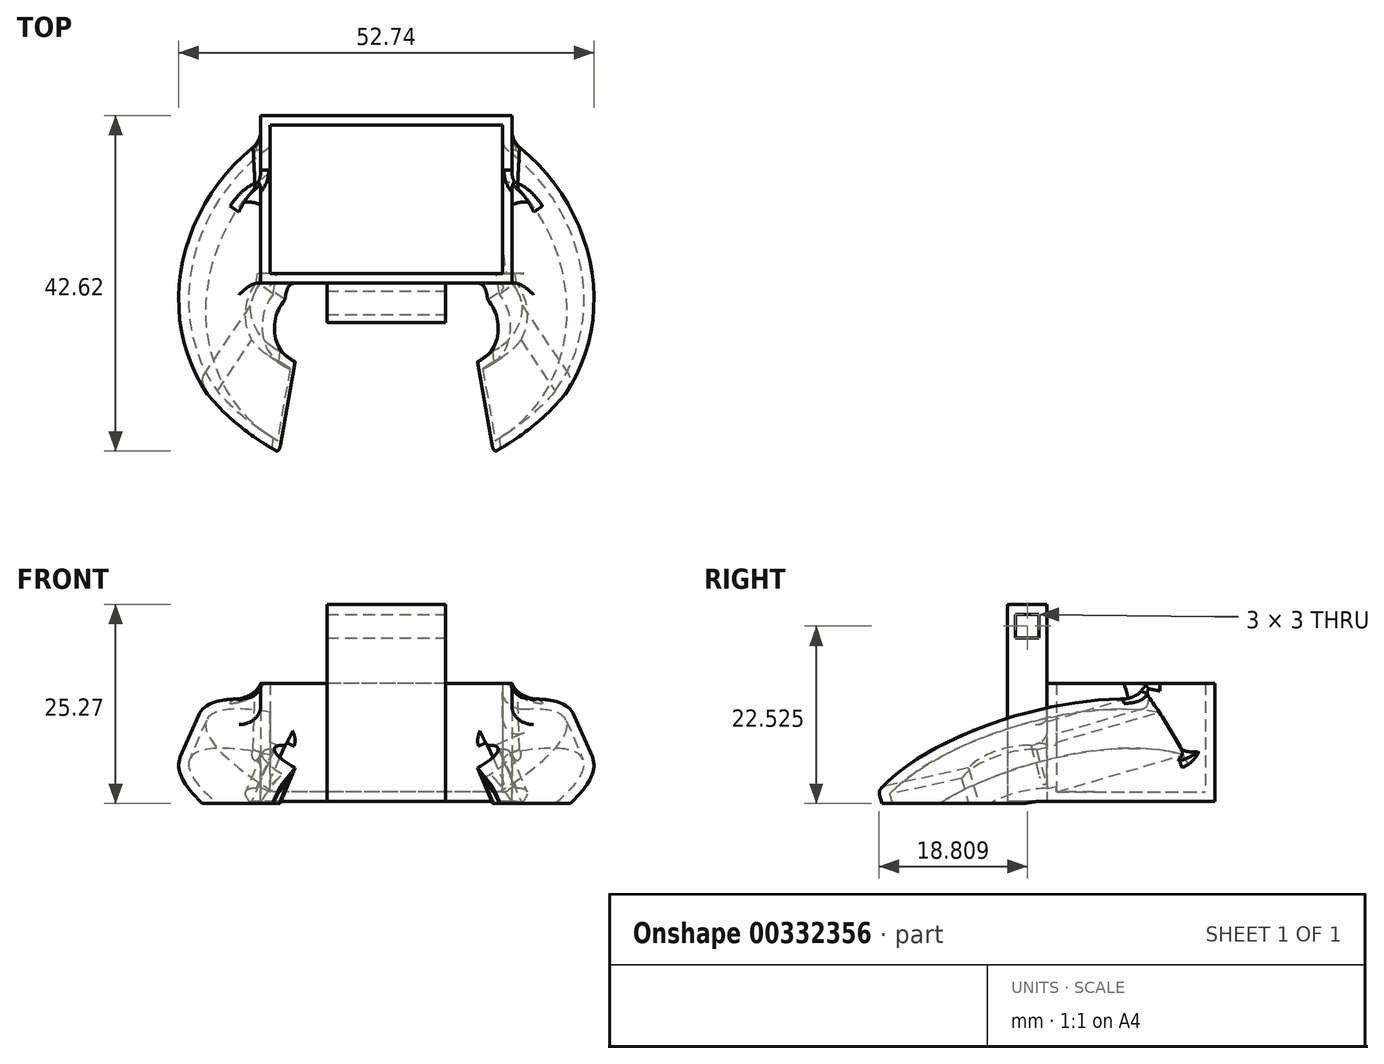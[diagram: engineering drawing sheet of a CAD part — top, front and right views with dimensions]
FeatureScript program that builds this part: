
annotation { "Feature Type Name" : "Feature", "Feature Type Description" : "" }
export const myFeature = defineFeature(function(context is Context, id is Id, definition is map)
    precondition{}
    {
        {
            var Q0;
            Q0=qCreatedBy(makeId("Top.planeOp"),FACE);
            var sketch = newSketch(context, id + "F0", { "sketchPlane" : qUnion([Q0])});
            skLineSegment(sketch, "E0.bottom", {"start": v(15.95, -10.65) * mm, "end": v(-15.95, -10.65) * mm});
            skLineSegment(sketch, "E0.top", {"start": v(15.95, 10.65) * mm, "end": v(-15.95, 10.65) * mm});
            skLineSegment(sketch, "E0.left", {"start": v(15.95, -10.65) * mm, "end": v(15.95, 10.65) * mm});
            skLineSegment(sketch, "E0.right", {"start": v(-15.95, -10.65) * mm, "end": v(-15.95, 10.65) * mm});
            skPoint(sketch, "E0.middle", {"position": v(0, 0) * mm});
            skLineSegment(sketch, "E1", {"start": v(-13, -24.65) * mm, "end": v(-13, -18.65) * mm});
            skLineSegment(sketch, "E2", {"start": v(-13, -24.65) * mm, "end": v(-13, -30.65) * mm});
            skLineSegment(sketch, "E3.MirrorCS", {"start": v(13, -24.65) * mm, "end": v(13, -18.65) * mm});
            skLineSegment(sketch, "E4.MirrorCS", {"start": v(13, -24.65) * mm, "end": v(13, -30.65) * mm});
            skArc(sketch, "E5", {"start": v(-15.95, -10.65) * mm, "mid": v(-16.46, -15.38) * mm, "end": v(-13, -18.65) * mm});
            skArc(sketch, "E6", {"start": v(-15.95, 10.65) * mm, "mid": v(-27.57, -10.94) * mm, "end": v(-13, -30.65) * mm});
            skArc(sketch, "E7.MirrorCS", {"start": v(15.95, 10.65) * mm, "mid": v(27.57, -10.94) * mm, "end": v(13, -30.65) * mm});
            skArc(sketch, "E8.MirrorCS", {"start": v(15.95, -10.65) * mm, "mid": v(16.46, -15.38) * mm, "end": v(13, -18.65) * mm});
            skSolve(sketch);
        }
        {
            var Q0;
            Q0=makeQuery(id+"F0.imprint","IMPRINT",FACE,{"disambiguationData":[TD([[makeQuery(id+"F0.imprint","IMPRINT",EDGE,{"derivedFrom":sQuery(id+"F0.wireOp",EDGE,"E0.bottom")}),-1.0]])]});
            extrude(context, id + "F1", {"entities" : qUnion([Q0]), "depth" : 15 * mm, "offsetDistance" : 25 * mm});
        }
        {
            var Q0;
            Q0=makeQuery(id+"F0.imprint","IMPRINT",FACE,{"disambiguationData":[TD([[makeQuery(id+"F0.imprint","IMPRINT",EDGE,{"derivedFrom":sQuery(id+"F0.wireOp",EDGE,"E0.right")}),1.0]])]});
            extrude(context, id + "F2", {"entities" : qUnion([Q0]), "depth" : 8 * mm, "offsetDistance" : 25 * mm});
        }
        {
            var Q0;
            Q0=makeQuery(id+"F2.opExtrude","SWEPT_BODY",BODY,{"disambiguationData":[OSD([sQuery(id+"F0.wireOp",EDGE,"E0.right"),sQuery(id+"F0.wireOp",EDGE,"E1"),sQuery(id+"F0.wireOp",EDGE,"E2"),sQuery(id+"F0.wireOp",EDGE,"GjkKXvnJ-jA0g-s26r-HWS4-I9semydN4EE0"),sQuery(id+"F0.wireOp",EDGE,"CBcXbAIJ-9305-cYkE-zvGn-Y6aC1Gbph8QT")])]});
            var Q1;
            Q1=sQuery(id+"F0.wireOp",EDGE,"E0.right");
            transform(context, id + "F3", {"entities" : qUnion([Q0]), "transformType" : TransformType.ROTATION, "transformAxis" : qUnion([Q1]), "angle" : 25 * degree, "makeCopy" : false});
        }
        {
            var Q0;
            Q0=makeQuery(id+"F2.opExtrude","SWEPT_BODY",BODY,{"disambiguationData":[OSD([sQuery(id+"F0.wireOp",EDGE,"E0.right"),sQuery(id+"F0.wireOp",EDGE,"E1"),sQuery(id+"F0.wireOp",EDGE,"E2"),sQuery(id+"F0.wireOp",EDGE,"QFbH83jj-XYne-KEbY-MEjT-L67cxlXek1Lr"),sQuery(id+"F0.wireOp",EDGE,"gXgNoo7v-niw8-iljs-8967-YQMKxby19gpY")])]});
            var Q1;
            Q1=sQuery(id+"F0.wireOp",EDGE,"E0.bottom");
            transform(context, id + "F4", {"entities" : qUnion([Q0]), "transformType" : TransformType.ROTATION, "transformAxis" : qUnion([Q1]), "angle" : -12 * degree, "makeCopy" : false});
        }
        {
            var Q0;
            Q0=makeQuery(id+"F2.opExtrude","SWEPT_BODY",BODY,{"disambiguationData":[OSD([sQuery(id+"F0.wireOp",EDGE,"E0.right"),sQuery(id+"F0.wireOp",EDGE,"E1"),sQuery(id+"F0.wireOp",EDGE,"E2"),sQuery(id+"F0.wireOp",EDGE,"E5"),sQuery(id+"F0.wireOp",EDGE,"E6")])]});
            var Q1;
            Q1=makeQuery(id+"F1.opExtrude","SWEPT_EDGE",EDGE,{"disambiguationData":[OSD([sQuery(id+"F0.wireOp",EDGE,"E0.bottom"),sQuery(id+"F0.wireOp",EDGE,"E0.right"),sQuery(id+"F0.wireOp",EDGE,"E5")])]});
            transform(context, id + "F5", {"entities" : qUnion([Q0]), "transformType" : TransformType.ROTATION, "transformAxis" : qUnion([Q1]), "angle" : 10 * degree, "makeCopy" : false});
        }
        {
            var Q0;
            Q0=makeQuery(id+"F2.opExtrude","SWEPT_BODY",BODY,{"disambiguationData":[OSD([sQuery(id+"F0.wireOp",EDGE,"E0.right"),sQuery(id+"F0.wireOp",EDGE,"E1"),sQuery(id+"F0.wireOp",EDGE,"E2"),sQuery(id+"F0.wireOp",EDGE,"GjkKXvnJ-jA0g-s26r-HWS4-I9semydN4EE0"),sQuery(id+"F0.wireOp",EDGE,"CBcXbAIJ-9305-cYkE-zvGn-Y6aC1Gbph8QT")])]});
            var Q1;
            Q1=qCreatedBy(makeId("Right.planeOp"),FACE);
            mirror(context, id + "F6", {"operationType" : NewBodyOperationType.ADD, "entities" : qUnion([Q0]), "mirrorPlane" : qUnion([Q1])});
        }
        {
            var Q0;
            Q0=makeQuery(id+"F1.opExtrude","CAP_FACE",FACE,{"disambiguationData":[OSD([sQuery(id+"F0.wireOp",EDGE,"E0.bottom"),sQuery(id+"F0.wireOp",EDGE,"E0.top"),sQuery(id+"F0.wireOp",EDGE,"E0.left"),sQuery(id+"F0.wireOp",EDGE,"E0.right")])],"isStart":false});
            var Q1;
            Q1=makeQuery(id+"F2.opExtrude","SWEPT_FACE",FACE,{"disambiguationData":[OSD([sQuery(id+"F0.wireOp",EDGE,"E1"),sQuery(id+"F0.wireOp",EDGE,"E2")])]});
            var Q2;
            Q2=makeQuery(id+"F6.opPattern","COPY",FACE,{"derivedFrom":makeQuery(id+"F2.opExtrude","SWEPT_FACE",FACE,{"disambiguationData":[OSD([sQuery(id+"F0.wireOp",EDGE,"E1"),sQuery(id+"F0.wireOp",EDGE,"E2")])]}),"instanceName":"1"});
            shell(context, id + "F7", {"entities" : qUnion([Q0, Q1, Q2]), "thickness" : 1.2 * mm});
        }
        {
            var Q0;
            {var subQ0=sQuery(id+"F0.wireOp",EDGE,"E0.right");Q0=makeQuery(id+"F7.opShell","OFFSET_EDGE",EDGE,{"disambiguationData":[OSD([subQ0]),TDD([makeQuery(id+"F6.opPattern","COPY",EDGE,{"derivedFrom":makeQuery(id+"F2.opExtrude","CAP_EDGE",EDGE,{"disambiguationData":[OSD([subQ0])],"isStart":true}),"instanceName":"1"})])]});}
            var Q1;
            {var subQ0=sQuery(id+"F0.wireOp",EDGE,"E0.right");Q1=makeQuery(id+"F7.opShell","OFFSET_EDGE",EDGE,{"disambiguationData":[OSD([subQ0]),TDD([makeQuery(id+"F2.opExtrude","CAP_EDGE",EDGE,{"disambiguationData":[OSD([subQ0])],"isStart":true})])]});}
            var Q2;
            {var subQ0=sQuery(id+"F0.wireOp",EDGE,"gXgNoo7v-niw8-iljs-8967-YQMKxby19gpY");var subQ1=sQuery(id+"F0.wireOp",EDGE,"QFbH83jj-XYne-KEbY-MEjT-L67cxlXek1Lr");var subQ2=sQuery(id+"F0.wireOp",EDGE,"E2");var subQ3=sQuery(id+"F0.wireOp",EDGE,"E1");var subQ4=sQuery(id+"F0.wireOp",EDGE,"E0.right");Q2=makeQuery(id+"F7.opShell","OFFSET_EDGE",EDGE,{"disambiguationData":[OSD([subQ4,subQ3,subQ2,subQ1,subQ0]),TDD([makeQuery(id+"F6.boolean.opBoolean","INTERSECT",EDGE,{"derivedFrom":[makeQuery(id+"F1.opExtrude","SWEPT_FACE",FACE,{"disambiguationData":[OSD([subQ4])]}),makeQuery(id+"F2.opExtrude","CAP_FACE",FACE,{"disambiguationData":[OSD([subQ4,subQ3,subQ2,subQ1,subQ0])],"isStart":false})]})])]});}
            var Q3;
            Q3=makeQuery(id+"F7.opShell","OFFSET_EDGE",EDGE,{"disambiguationData":[OSD([sQuery(id+"F0.wireOp",EDGE,"E0.left"),sQuery(id+"F0.wireOp",EDGE,"E0.right"),sQuery(id+"F0.wireOp",EDGE,"E1"),sQuery(id+"F0.wireOp",EDGE,"E2"),sQuery(id+"F0.wireOp",EDGE,"QFbH83jj-XYne-KEbY-MEjT-L67cxlXek1Lr"),sQuery(id+"F0.wireOp",EDGE,"gXgNoo7v-niw8-iljs-8967-YQMKxby19gpY")])]});
            fillet(context, id + "F8", {"entities" : qUnion([Q0, Q1, Q2, Q3]), "tangentPropagation" : true, "radius" : 2 * mm, "defaultsChanged" : true, "vertexSettings" : [], "allowEdgeOverflow" : false});
        }
        {
            var Q0;
            Q0=makeQuery(id+"F0.imprint","IMPRINT",FACE,{"disambiguationData":[TD([[makeQuery(id+"F0.imprint","IMPRINT",EDGE,{"derivedFrom":sQuery(id+"F0.wireOp",EDGE,"E0.bottom")}),-1.0]])]});
            var sketch = newSketch(context, id + "F9", { "sketchPlane" : qUnion([Q0])});
            skLineSegment(sketch, "E9.bottom", {"start": v(7.54, -10.65) * mm, "end": v(-7.54, -10.65) * mm});
            skLineSegment(sketch, "E9.top", {"start": v(7.54, -15.65) * mm, "end": v(-7.54, -15.65) * mm});
            skLineSegment(sketch, "E9.left", {"start": v(7.54, -10.65) * mm, "end": v(7.54, -15.65) * mm});
            skLineSegment(sketch, "E9.right", {"start": v(-7.54, -10.65) * mm, "end": v(-7.54, -15.65) * mm});
            skPoint(sketch, "E9.middle", {"position": v(0, -13.15) * mm});
            skSolve(sketch);
        }
        {
            var Q0;
            {var subQ0=sQuery(id+"F9.wireOp",EDGE,"E9.top");Q0=makeQuery(id+"F9.imprint","IMPRINT",FACE,{"disambiguationData":[TD([[makeQuery(id+"F9.imprint","IMPRINT",EDGE,{"derivedFrom":subQ0}),-1.0]])]});}
            extrude(context, id + "F10", {"entities" : qUnion([Q0]), "operationType" : NewBodyOperationType.ADD, "depth" : 25 * mm, "offsetDistance" : 25 * mm});
        }
        {
            var Q0;
            Q0=makeQuery(id+"F10.opExtrude","SWEPT_FACE",FACE,{"disambiguationData":[OSD([sQuery(id+"F9.wireOp",EDGE,"E9.left")])]});
            var sketch = newSketch(context, id + "F11", { "sketchPlane" : qUnion([Q0])});
            skLineSegment(sketch, "E10.bottom", {"start": v(-11.66, 20.76) * mm, "end": v(-14.66, 20.76) * mm});
            skLineSegment(sketch, "E10.top", {"start": v(-11.66, 23.76) * mm, "end": v(-14.66, 23.76) * mm});
            skLineSegment(sketch, "E10.left", {"start": v(-11.66, 20.76) * mm, "end": v(-11.66, 23.76) * mm});
            skLineSegment(sketch, "E10.right", {"start": v(-14.66, 20.76) * mm, "end": v(-14.66, 23.76) * mm});
            skPoint(sketch, "E10.middle", {"position": v(-13.16, 22.26) * mm});
            skSolve(sketch);
        }
        {
            var Q0;
            Q0=makeQuery(id+"F11.imprint","IMPRINT",FACE,{"disambiguationData":[TD([[makeQuery(id+"F11.imprint","IMPRINT",EDGE,{"derivedFrom":sQuery(id+"F11.wireOp",EDGE,"E10.bottom")}),-1.0]])]});
            extrude(context, id + "F12", {"entities" : qUnion([Q0]), "operationType" : NewBodyOperationType.REMOVE, "oppositeDirection" : true, "depth" : 25 * mm, "offsetDistance" : 25 * mm});
        }
        {
            var Q0;
            Q0=makeQuery(id+"F6.boolean.opBoolean","INTERSECT",EDGE,{"derivedFrom":[makeQuery(id+"F1.opExtrude","SWEPT_FACE",FACE,{"disambiguationData":[OSD([sQuery(id+"F0.wireOp",EDGE,"E0.left")])]}),makeQuery(id+"F6.opPattern","COPY",FACE,{"derivedFrom":makeQuery(id+"F2.opExtrude","CAP_FACE",FACE,{"disambiguationData":[OSD([sQuery(id+"F0.wireOp",EDGE,"E0.right"),sQuery(id+"F0.wireOp",EDGE,"E1"),sQuery(id+"F0.wireOp",EDGE,"E2"),sQuery(id+"F0.wireOp",EDGE,"E5"),sQuery(id+"F0.wireOp",EDGE,"E6")])],"isStart":false}),"instanceName":"1"})]});
            var Q1;
            Q1=makeQuery(id+"F6.boolean.opBoolean","INTERSECT",EDGE,{"derivedFrom":[makeQuery(id+"F1.opExtrude","SWEPT_FACE",FACE,{"disambiguationData":[OSD([sQuery(id+"F0.wireOp",EDGE,"E0.left")])]}),makeQuery(id+"F6.opPattern","COPY",FACE,{"derivedFrom":makeQuery(id+"F2.opExtrude","SWEPT_FACE",FACE,{"disambiguationData":[OSD([sQuery(id+"F0.wireOp",EDGE,"E6")])]}),"instanceName":"1"})]});
            var Q2;
            Q2=makeQuery(id+"F6.boolean.opBoolean","INTERSECT",EDGE,{"derivedFrom":[makeQuery(id+"F1.opExtrude","SWEPT_FACE",FACE,{"disambiguationData":[OSD([sQuery(id+"F0.wireOp",EDGE,"E0.bottom")])]}),makeQuery(id+"F6.opPattern","COPY",FACE,{"derivedFrom":makeQuery(id+"F2.opExtrude","CAP_FACE",FACE,{"disambiguationData":[OSD([sQuery(id+"F0.wireOp",EDGE,"E0.right"),sQuery(id+"F0.wireOp",EDGE,"E1"),sQuery(id+"F0.wireOp",EDGE,"E2"),sQuery(id+"F0.wireOp",EDGE,"E5"),sQuery(id+"F0.wireOp",EDGE,"E6")])],"isStart":false}),"instanceName":"1"})]});
            var Q3;
            Q3=makeQuery(id+"F6.boolean.opBoolean","INTERSECT",EDGE,{"derivedFrom":[makeQuery(id+"F1.opExtrude","SWEPT_FACE",FACE,{"disambiguationData":[OSD([sQuery(id+"F0.wireOp",EDGE,"E0.bottom")])]}),makeQuery(id+"F2.opExtrude","CAP_FACE",FACE,{"disambiguationData":[OSD([sQuery(id+"F0.wireOp",EDGE,"E0.right"),sQuery(id+"F0.wireOp",EDGE,"E1"),sQuery(id+"F0.wireOp",EDGE,"E2"),sQuery(id+"F0.wireOp",EDGE,"E5"),sQuery(id+"F0.wireOp",EDGE,"E6")])],"isStart":false})]});
            var Q4;
            {var subQ0=sQuery(id+"F0.wireOp",EDGE,"E0.right");Q4=makeQuery(id+"F6.boolean.opBoolean","INTERSECT",EDGE,{"derivedFrom":[makeQuery(id+"F1.opExtrude","SWEPT_FACE",FACE,{"disambiguationData":[OSD([subQ0])]}),makeQuery(id+"F2.opExtrude","CAP_FACE",FACE,{"disambiguationData":[OSD([subQ0,sQuery(id+"F0.wireOp",EDGE,"E1"),sQuery(id+"F0.wireOp",EDGE,"E2"),sQuery(id+"F0.wireOp",EDGE,"E5"),sQuery(id+"F0.wireOp",EDGE,"E6")])],"isStart":false})]});}
            var Q5;
            Q5=makeQuery(id+"F6.boolean.opBoolean","INTERSECT",EDGE,{"derivedFrom":[makeQuery(id+"F1.opExtrude","SWEPT_FACE",FACE,{"disambiguationData":[OSD([sQuery(id+"F0.wireOp",EDGE,"E0.right")])]}),makeQuery(id+"F2.opExtrude","SWEPT_FACE",FACE,{"disambiguationData":[OSD([sQuery(id+"F0.wireOp",EDGE,"E6")])]})]});
            fillet(context, id + "F13", {"entities" : qUnion([Q0, Q1, Q2, Q3, Q4, Q5]), "tangentPropagation" : true, "radius" : 2 * mm, "defaultsChanged" : false, "vertexSettings" : [], "allowEdgeOverflow" : false});
        }
        {
            var Q0;
            Q0=makeQuery(id+"F6.boolean.opBoolean","INTERSECT",EDGE,{"derivedFrom":[makeQuery(id+"F1.opExtrude","SWEPT_FACE",FACE,{"disambiguationData":[OSD([sQuery(id+"F0.wireOp",EDGE,"E0.left")])]}),makeQuery(id+"F6.opPattern","COPY",FACE,{"derivedFrom":makeQuery(id+"F2.opExtrude","CAP_FACE",FACE,{"disambiguationData":[OSD([sQuery(id+"F0.wireOp",EDGE,"E0.right"),sQuery(id+"F0.wireOp",EDGE,"E1"),sQuery(id+"F0.wireOp",EDGE,"E2"),sQuery(id+"F0.wireOp",EDGE,"E5"),sQuery(id+"F0.wireOp",EDGE,"E6")])],"isStart":true}),"instanceName":"1"})]});
            var Q1;
            Q1=makeQuery(id+"F6.boolean.opBoolean","INTERSECT",EDGE,{"derivedFrom":[makeQuery(id+"F1.opExtrude","SWEPT_FACE",FACE,{"disambiguationData":[OSD([sQuery(id+"F0.wireOp",EDGE,"E0.bottom")])]}),makeQuery(id+"F6.opPattern","COPY",FACE,{"derivedFrom":makeQuery(id+"F2.opExtrude","SWEPT_FACE",FACE,{"disambiguationData":[OSD([sQuery(id+"F0.wireOp",EDGE,"E0.right")])]}),"instanceName":"1"})]});
            var Q2;
            Q2=makeQuery(id+"F6.boolean.opBoolean","INTERSECT",EDGE,{"derivedFrom":[makeQuery(id+"F1.opExtrude","SWEPT_FACE",FACE,{"disambiguationData":[OSD([sQuery(id+"F0.wireOp",EDGE,"E0.bottom")])]}),makeQuery(id+"F2.opExtrude","SWEPT_FACE",FACE,{"disambiguationData":[OSD([sQuery(id+"F0.wireOp",EDGE,"E0.right")])]})]});
            var Q3;
            {var subQ0=sQuery(id+"F0.wireOp",EDGE,"E0.right");Q3=makeQuery(id+"F6.boolean.opBoolean","INTERSECT",EDGE,{"derivedFrom":[makeQuery(id+"F1.opExtrude","SWEPT_FACE",FACE,{"disambiguationData":[OSD([subQ0])]}),makeQuery(id+"F2.opExtrude","CAP_FACE",FACE,{"disambiguationData":[OSD([subQ0,sQuery(id+"F0.wireOp",EDGE,"E1"),sQuery(id+"F0.wireOp",EDGE,"E2"),sQuery(id+"F0.wireOp",EDGE,"E5"),sQuery(id+"F0.wireOp",EDGE,"E6")])],"isStart":true})]});}
            var Q4;
            Q4=makeQuery(id+"F6.opPattern","COPY",EDGE,{"derivedFrom":makeQuery(id+"F2.opExtrude","CAP_EDGE",EDGE,{"disambiguationData":[OSD([sQuery(id+"F0.wireOp",EDGE,"E6")])],"isStart":false}),"instanceName":"1"});
            var Q5;
            Q5=makeQuery(id+"F6.opPattern","COPY",EDGE,{"derivedFrom":makeQuery(id+"F2.opExtrude","CAP_EDGE",EDGE,{"disambiguationData":[OSD([sQuery(id+"F0.wireOp",EDGE,"E6")])],"isStart":true}),"instanceName":"1"});
            var Q6;
            Q6=makeQuery(id+"F2.opExtrude","CAP_EDGE",EDGE,{"disambiguationData":[OSD([sQuery(id+"F0.wireOp",EDGE,"E6")])],"isStart":false});
            var Q7;
            Q7=makeQuery(id+"F2.opExtrude","CAP_EDGE",EDGE,{"disambiguationData":[OSD([sQuery(id+"F0.wireOp",EDGE,"E6")])],"isStart":true});
            fillet(context, id + "F14", {"entities" : qUnion([Q0, Q1, Q2, Q3, Q4, Q5, Q6, Q7]), "tangentPropagation" : true, "radius" : 1 * mm, "defaultsChanged" : false, "vertexSettings" : [], "allowEdgeOverflow" : false});
        }
        {
            var Q0;
            Q0=qCreatedBy(makeId("Front.planeOp"),FACE);
            var sketch = newSketch(context, id + "F15", { "sketchPlane" : qUnion([Q0])});
            skLineSegment(sketch, "E11.bottom", {"start": v(27.74, -0.27) * mm, "end": v(-27.74, -0.27) * mm});
            skLineSegment(sketch, "E11.top", {"start": v(27.74, -35.02) * mm, "end": v(-27.74, -35.02) * mm});
            skLineSegment(sketch, "E11.left", {"start": v(27.74, -0.27) * mm, "end": v(27.74, -35.02) * mm});
            skLineSegment(sketch, "E11.right", {"start": v(-27.74, -0.27) * mm, "end": v(-27.74, -35.02) * mm});
            skPoint(sketch, "E11.middle", {"position": v(0, -17.64) * mm});
            skSolve(sketch);
        }
        {
            var Q0;
            Q0=makeQuery(id+"F15.imprint","IMPRINT",FACE,{"disambiguationData":[TD([[makeQuery(id+"F15.imprint","IMPRINT",EDGE,{"derivedFrom":sQuery(id+"F15.wireOp",EDGE,"E11.bottom")}),1.0]])]});
            extrude(context, id + "F16", {"entities" : qUnion([Q0]), "operationType" : NewBodyOperationType.REMOVE, "depth" : 35 * mm, "offsetDistance" : 25 * mm});
        }
    });
